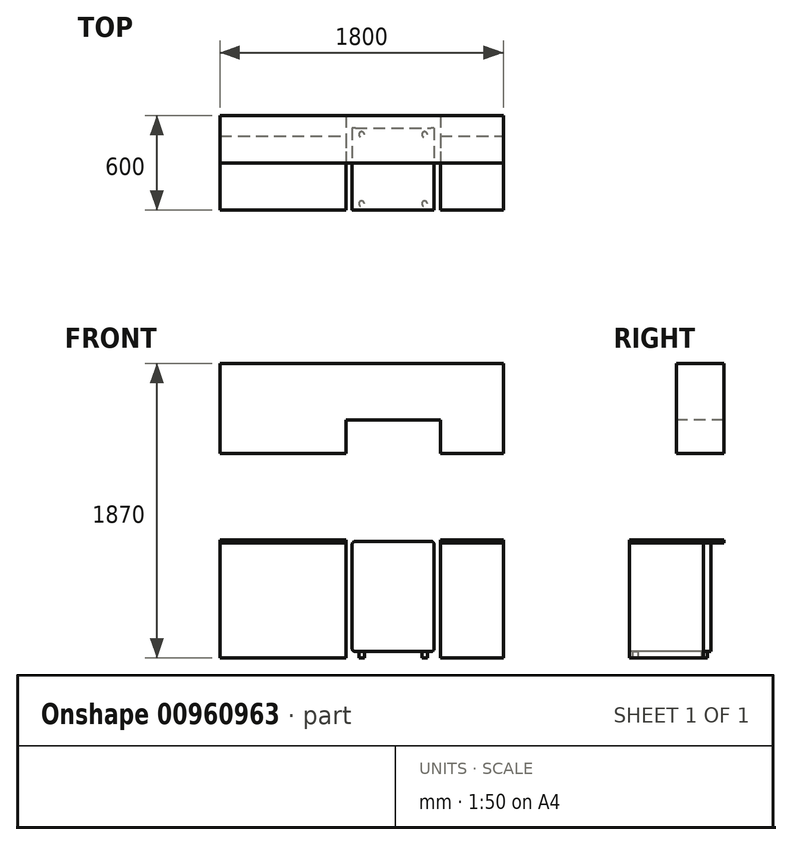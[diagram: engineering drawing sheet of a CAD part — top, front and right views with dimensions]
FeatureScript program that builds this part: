
annotation { "Feature Type Name" : "Feature", "Feature Type Description" : "" }
export const myFeature = defineFeature(function(context is Context, id is Id, definition is map)
    precondition{}
    {
        {
            var Q0;
            Q0=qCreatedBy(makeId("Front.planeOp"),FACE);
            var sketch = newSketch(context, id + "F0", { "sketchPlane" : qUnion([Q0])});
            skLineSegment(sketch, "E0.bottom", {"start": v(-900, 935) * mm, "end": v(900, 935) * mm});
            skLineSegment(sketch, "E0.top", {"start": v(-900, -935) * mm, "end": v(-100, -935) * mm});
            skLineSegment(sketch, "E0.left", {"start": v(-900, 935) * mm, "end": v(-900, 365) * mm});
            skLineSegment(sketch, "E0.right", {"start": v(900, 935) * mm, "end": v(900, 365) * mm});
            skPoint(sketch, "E0.middle", {"position": v(0, 0) * mm});
            skLineSegment(sketch, "E1.bottom", {"start": v(-900, 365) * mm, "end": v(-100, 365) * mm});
            skLineSegment(sketch, "E1.top", {"start": v(-900, -185) * mm, "end": v(-100, -185) * mm});
            skLineSegment(sketch, "E2", {"start": v(-100, 935) * mm, "end": v(-100, 365) * mm});
            skLineSegment(sketch, "E3", {"start": v(500, 935) * mm, "end": v(500, 365) * mm});
            skLineSegment(sketch, "E4.trimOffspring", {"start": v(900, -185) * mm, "end": v(900, -935) * mm});
            skLineSegment(sketch, "E5.trimOffspring", {"start": v(500, -185) * mm, "end": v(500, -935) * mm});
            skLineSegment(sketch, "E6.trimOffspring", {"start": v(-100, -185) * mm, "end": v(-100, -935) * mm});
            skLineSegment(sketch, "E7.trimOffspring", {"start": v(-900, -185) * mm, "end": v(-900, -935) * mm});
            skLineSegment(sketch, "E8.trimOffspring", {"start": v(500, 365) * mm, "end": v(900, 365) * mm});
            skPoint(sketch, "E9", {"position": v(-500, 365) * mm});
            skLineSegment(sketch, "E10", {"start": v(-500, 365) * mm, "end": v(-500, 935) * mm});
            skLineSegment(sketch, "E11", {"start": v(-500, -205) * mm, "end": v(-500, -935) * mm});
            skPoint(sketch, "E12", {"position": v(-500, -185) * mm});
            skLineSegment(sketch, "E13.0", {"start": v(-900, -205) * mm, "end": v(-100, -205) * mm});
            skPoint(sketch, "E14", {"position": v(-500, -205) * mm});
            skPoint(sketch, "E15", {"position": v(-100, -205) * mm});
            skPoint(sketch, "E16", {"position": v(500, -205) * mm});
            skPoint(sketch, "E17", {"position": v(-100, -185) * mm});
            skPoint(sketch, "E18", {"position": v(500, -185) * mm});
            skLineSegment(sketch, "E19.trimOffspring", {"start": v(500, -185) * mm, "end": v(900, -185) * mm});
            skLineSegment(sketch, "E20.trimOffspring", {"start": v(500, -205) * mm, "end": v(900, -205) * mm});
            skLineSegment(sketch, "E21.trimOffspring", {"start": v(500, -935) * mm, "end": v(900, -935) * mm});
            skPoint(sketch, "E22.orphan", {"position": v(500, -221.75) * mm});
            skLineSegment(sketch, "E23", {"start": v(-40, -194.12) * mm, "end": v(440, -194.12) * mm});
            skLineSegment(sketch, "E24.0", {"start": v(-60, -214.12) * mm, "end": v(460, -214.12) * mm});
            skLineSegment(sketch, "E25", {"start": v(-60, -214.12) * mm, "end": v(-60, -875) * mm});
            skLineSegment(sketch, "E26", {"start": v(460, -214.12) * mm, "end": v(460, -875) * mm});
            skPoint(sketch, "E27.orphan", {"position": v(500, -194.12) * mm});
            skPoint(sketch, "E28", {"position": v(-60, -214.12) * mm});
            skPoint(sketch, "E29", {"position": v(460, -214.12) * mm});
            skArc(sketch, "E30.filletArc", {"start": v(-40, -194.12) * mm, "mid": v(-54.14, -199.98) * mm, "end": v(-60, -214.12) * mm});
            skArc(sketch, "E31.filletArc", {"start": v(460, -214.12) * mm, "mid": v(454.14, -199.98) * mm, "end": v(440, -194.12) * mm});
            skLineSegment(sketch, "E32", {"start": v(-60, -335.2) * mm, "end": v(460, -335.2) * mm});
            skLineSegment(sketch, "E33", {"start": v(-100, 575) * mm, "end": v(500, 575) * mm});
            skLineSegment(sketch, "E34", {"start": v(-40, -895) * mm, "end": v(440, -895) * mm});
            skLineSegment(sketch, "E35", {"start": v(-60, -776.44) * mm, "end": v(460, -776.44) * mm});
            skArc(sketch, "E36.filletArc", {"start": v(-60, -875) * mm, "mid": v(-54.14, -889.14) * mm, "end": v(-40, -895) * mm});
            skArc(sketch, "E37.filletArc", {"start": v(440, -895) * mm, "mid": v(454.14, -889.14) * mm, "end": v(460, -875) * mm});
            skSolve(sketch);
        }
        {
            var Q0;
            {var subQ0=sQuery(id+"F0.wireOp",EDGE,"E24.0");Q0=makeQuery(id+"F0.imprint","IMPRINT",FACE,{"disambiguationData":[TD([[makeQuery(id+"F0.imprint","IMPRINT",EDGE,{"derivedFrom":subQ0}),-1.0]])]});}
            var Q1;
            {var subQ0=sQuery(id+"F0.wireOp",EDGE,"E32");Q1=makeQuery(id+"F0.imprint","IMPRINT",FACE,{"disambiguationData":[TD([[makeQuery(id+"F0.imprint","IMPRINT",EDGE,{"derivedFrom":subQ0}),-1.0]])]});}
            var Q2;
            Q2=makeQuery(id+"F0.imprint","IMPRINT",FACE,{"disambiguationData":[TD([[makeQuery(id+"F0.imprint","IMPRINT",EDGE,{"derivedFrom":sQuery(id+"F0.wireOp",EDGE,"E23")}),-1.0]])]});
            var Q3;
            Q3=makeQuery(id+"F0.imprint","IMPRINT",FACE,{"disambiguationData":[TD([[makeQuery(id+"F0.imprint","IMPRINT",EDGE,{"derivedFrom":sQuery(id+"F0.wireOp",EDGE,"E34")}),1.0]])]});
            extrude(context, id + "F1", {"entities" : qUnion([Q0, Q1, Q2, Q3]), "depth" : -520 * mm, "offsetDistance" : 25 * mm});
        }
        {
            var Q0;
            {var subQ4=sQuery(id+"F0.wireOp",EDGE,"E1.top");Q0=makeQuery(id+"F0.imprint","IMPRINT",FACE,{"disambiguationData":[TD([[makeQuery(id+"F0.imprint","IMPRINT",EDGE,{"derivedFrom":subQ4}),-1.0]])]});}
            var Q1;
            {var subQ0=sQuery(id+"F0.wireOp",EDGE,"E19.trimOffspring");Q1=makeQuery(id+"F0.imprint","IMPRINT",FACE,{"disambiguationData":[TD([[makeQuery(id+"F0.imprint","IMPRINT",EDGE,{"derivedFrom":subQ0}),-1.0]])]});}
            extrude(context, id + "F2", {"entities" : qUnion([Q0, Q1]), "oppositeDirection" : true, "depth" : 600 * mm, "offsetDistance" : 25 * mm});
        }
        {
            var Q0;
            {var subQ3=sQuery(id+"F0.wireOp",EDGE,"E11");Q0=makeQuery(id+"F0.imprint","IMPRINT",FACE,{"disambiguationData":[TD([[makeQuery(id+"F0.imprint","IMPRINT",EDGE,{"derivedFrom":subQ3}),-1.0]])]});}
            var Q1;
            {var subQ3=sQuery(id+"F0.wireOp",EDGE,"E11");Q1=makeQuery(id+"F0.imprint","IMPRINT",FACE,{"disambiguationData":[TD([[makeQuery(id+"F0.imprint","IMPRINT",EDGE,{"derivedFrom":subQ3}),1.0]])]});}
            var Q2;
            {var subQ2=sQuery(id+"F0.wireOp",EDGE,"E20.trimOffspring");Q2=makeQuery(id+"F0.imprint","IMPRINT",FACE,{"disambiguationData":[TD([[makeQuery(id+"F0.imprint","IMPRINT",EDGE,{"derivedFrom":subQ2}),-1.0]])]});}
            extrude(context, id + "F3", {"entities" : qUnion([Q0, Q1, Q2]), "oppositeDirection" : true, "depth" : 470 * mm, "offsetDistance" : 25 * mm});
        }
        {
            var Q0;
            {var subQ0=sQuery(id+"F0.wireOp",EDGE,"E0.left");Q0=makeQuery(id+"F0.imprint","IMPRINT",FACE,{"disambiguationData":[TD([[makeQuery(id+"F0.imprint","IMPRINT",EDGE,{"derivedFrom":subQ0}),1.0]])]});}
            var Q1;
            {var subQ6=sQuery(id+"F0.wireOp",EDGE,"E10");Q1=makeQuery(id+"F0.imprint","IMPRINT",FACE,{"disambiguationData":[TD([[makeQuery(id+"F0.imprint","IMPRINT",EDGE,{"derivedFrom":subQ6}),-1.0]])]});}
            var Q2;
            {var subQ5=sQuery(id+"F0.wireOp",EDGE,"E33");Q2=makeQuery(id+"F0.imprint","IMPRINT",FACE,{"disambiguationData":[TD([[makeQuery(id+"F0.imprint","IMPRINT",EDGE,{"derivedFrom":subQ5}),1.0]])]});}
            var Q3;
            {var subQ3=sQuery(id+"F0.wireOp",EDGE,"E0.right");Q3=makeQuery(id+"F0.imprint","IMPRINT",FACE,{"disambiguationData":[TD([[makeQuery(id+"F0.imprint","IMPRINT",EDGE,{"derivedFrom":subQ3}),-1.0]])]});}
            extrude(context, id + "F4", {"entities" : qUnion([Q0, Q1, Q2, Q3]), "oppositeDirection" : true, "depth" : 600 * mm, "hasOffset" : true, "offsetDistance" : 300 * mm, "hasSecondDirection" : true, "secondDirectionOppositeDirection" : true, "secondDirectionDepth" : 300 * mm});
        }
        {
            var Q0;
            Q0=makeQuery(id+"F1.opExtrude","SWEPT_FACE",FACE,{"disambiguationData":[OSD([sQuery(id+"F0.wireOp",EDGE,"E34")])]});
            var sketch = newSketch(context, id + "F5", { "sketchPlane" : qUnion([Q0])});
            skLineSegment(sketch, "E38.0", {"start": v(382.5, -40) * mm, "end": v(17.5, -40) * mm});
            skLineSegment(sketch, "E38.1", {"start": v(400, -462.5) * mm, "end": v(400, -57.5) * mm});
            skLineSegment(sketch, "E38.2", {"start": v(17.5, -480) * mm, "end": v(382.5, -480) * mm});
            skLineSegment(sketch, "E38.3", {"start": v(0, -57.5) * mm, "end": v(0, -462.5) * mm});
            skLineSegment(sketch, "E39.0", {"start": v(435, -5) * mm, "end": v(-35, -5) * mm});
            skLineSegment(sketch, "E39.1", {"start": v(435, -515) * mm, "end": v(435, -5) * mm});
            skLineSegment(sketch, "E39.2", {"start": v(-35, -515) * mm, "end": v(435, -515) * mm});
            skLineSegment(sketch, "E39.3", {"start": v(-35, -5) * mm, "end": v(-35, -515) * mm});
            skCircle(sketch, "E40", {"center": v(0, -40) * mm, "radius": 17.5 * mm});
            skCircle(sketch, "E41", {"center": v(400, -40) * mm, "radius": 17.5 * mm});
            skCircle(sketch, "E42", {"center": v(0, -480) * mm, "radius": 17.5 * mm});
            skCircle(sketch, "E43", {"center": v(400, -480) * mm, "radius": 17.5 * mm});
            skSolve(sketch);
        }
        {
            var Q0;
            {var subQ0=sQuery(id+"F5.wireOp",EDGE,"E40");var subQ1=makeQuery(id+"F5.imprint","INTERSECT",VERTEX,{"derivedFrom":[sQuery(id+"F5.wireOp",EDGE,"E38.0"),subQ0]});Q0=makeQuery(id+"F5.imprint","IMPRINT",FACE,{"disambiguationData":[TD([[makeQuery(id+"F5.imprint","IMPRINT",EDGE,{"disambiguationData":[TD([[subQ1,-1.0]])],"derivedFrom":subQ0}),1.0]])]});}
            var Q1;
            {var subQ0=sQuery(id+"F5.wireOp",EDGE,"E41");var subQ1=makeQuery(id+"F5.imprint","INTERSECT",VERTEX,{"derivedFrom":[sQuery(id+"F5.wireOp",EDGE,"E38.0"),subQ0]});Q1=makeQuery(id+"F5.imprint","IMPRINT",FACE,{"disambiguationData":[TD([[makeQuery(id+"F5.imprint","IMPRINT",EDGE,{"disambiguationData":[TD([[subQ1,-1.0]])],"derivedFrom":subQ0}),1.0]])]});}
            var Q2;
            {var subQ0=sQuery(id+"F5.wireOp",EDGE,"E42");var subQ1=makeQuery(id+"F5.imprint","INTERSECT",VERTEX,{"derivedFrom":[sQuery(id+"F5.wireOp",EDGE,"E38.2"),subQ0]});Q2=makeQuery(id+"F5.imprint","IMPRINT",FACE,{"disambiguationData":[TD([[makeQuery(id+"F5.imprint","IMPRINT",EDGE,{"disambiguationData":[TD([[subQ1,-1.0]])],"derivedFrom":subQ0}),1.0]])]});}
            var Q3;
            {var subQ0=sQuery(id+"F5.wireOp",EDGE,"E43");var subQ1=makeQuery(id+"F5.imprint","INTERSECT",VERTEX,{"derivedFrom":[sQuery(id+"F5.wireOp",EDGE,"E38.1"),subQ0]});Q3=makeQuery(id+"F5.imprint","IMPRINT",FACE,{"disambiguationData":[TD([[makeQuery(id+"F5.imprint","IMPRINT",EDGE,{"disambiguationData":[TD([[subQ1,-1.0]])],"derivedFrom":subQ0}),1.0]])]});}
            extrude(context, id + "F6", {"entities" : qUnion([Q0, Q1, Q2, Q3]), "operationType" : NewBodyOperationType.ADD, "depth" : 40 * mm, "offsetDistance" : 25 * mm});
        }
    });
